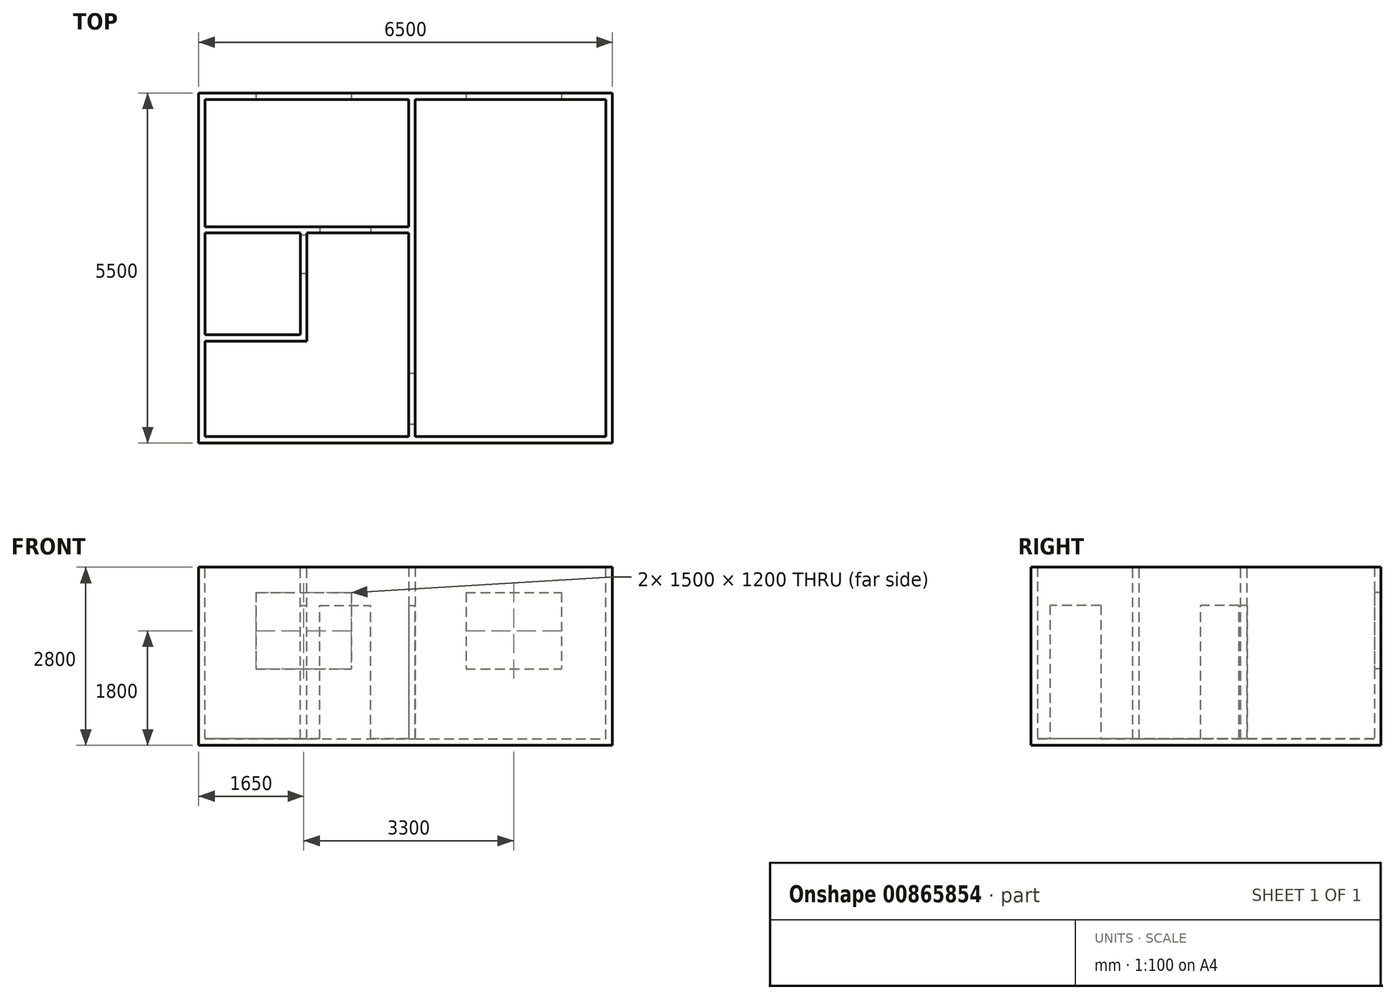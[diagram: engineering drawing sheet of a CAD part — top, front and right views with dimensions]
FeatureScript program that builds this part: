
annotation { "Feature Type Name" : "Feature", "Feature Type Description" : "" }
export const myFeature = defineFeature(function(context is Context, id is Id, definition is map)
    precondition{}
    {
        {
            var Q0;
            Q0=qCreatedBy(makeId("Top.planeOp"),FACE);
            var sketch = newSketch(context, id + "F0", { "sketchPlane" : qUnion([Q0])});
            skLineSegment(sketch, "E0", {"start": v(-6500, 5500) * mm, "end": v(0, 5500) * mm});
            skLineSegment(sketch, "E1", {"start": v(0, 5500) * mm, "end": v(0, 0) * mm});
            skLineSegment(sketch, "E2", {"start": v(0, 0) * mm, "end": v(-6500, 0) * mm});
            skLineSegment(sketch, "E3", {"start": v(-6500, 0) * mm, "end": v(-6500, 5500) * mm});
            skSolve(sketch);
        }
        {
            var Q0;
            Q0=makeQuery(id+"F0.imprint","IMPRINT",FACE,{"disambiguationData":[TD([[makeQuery(id+"F0.imprint","IMPRINT",EDGE,{"derivedFrom":sQuery(id+"F0.wireOp",EDGE,"E0")}),-1.0]])]});
            extrude(context, id + "F1", {"entities" : qUnion([Q0]), "depth" : 2800 * mm, "offsetDistance" : 25 * mm});
        }
        {
            var Q0;
            Q0=makeQuery(id+"F1.opExtrude","CAP_FACE",FACE,{"disambiguationData":[OSD([sQuery(id+"F0.wireOp",EDGE,"E0"),sQuery(id+"F0.wireOp",EDGE,"E1"),sQuery(id+"F0.wireOp",EDGE,"E2"),sQuery(id+"F0.wireOp",EDGE,"E3")])],"isStart":false});
            var sketch = newSketch(context, id + "F2", { "sketchPlane" : qUnion([Q0])});
            skLineSegment(sketch, "E4.bottom", {"start": v(-6400, 5400) * mm, "end": v(-100, 5400) * mm});
            skLineSegment(sketch, "E4.top", {"start": v(-6400, 100) * mm, "end": v(-100, 100) * mm});
            skLineSegment(sketch, "E4.left", {"start": v(-6400, 5400) * mm, "end": v(-6400, 100) * mm});
            skLineSegment(sketch, "E4.right", {"start": v(-100, 5400) * mm, "end": v(-100, 100) * mm});
            skSolve(sketch);
        }
        {
            var Q0;
            Q0=makeQuery(id+"F2.imprint","IMPRINT",FACE,{"disambiguationData":[TD([[makeQuery(id+"F2.imprint","IMPRINT",EDGE,{"derivedFrom":sQuery(id+"F2.wireOp",EDGE,"E4.bottom")}),-1.0]])]});
            extrude(context, id + "F3", {"entities" : qUnion([Q0]), "operationType" : NewBodyOperationType.REMOVE, "oppositeDirection" : true, "depth" : 2700 * mm, "offsetDistance" : 25 * mm});
        }
        {
            var Q0;
            Q0=makeQuery(id+"F3.boolean.opBoolean","COPY",FACE,{"derivedFrom":makeQuery(id+"F3.opExtrude","SWEPT_FACE",FACE,{"disambiguationData":[OSD([sQuery(id+"F2.wireOp",EDGE,"E4.bottom")])]})});
            var sketch = newSketch(context, id + "F4", { "sketchPlane" : qUnion([Q0])});
            skLineSegment(sketch, "E5.bottom", {"start": v(-3200, 2800) * mm, "end": v(-3100, 2800) * mm});
            skLineSegment(sketch, "E5.top", {"start": v(-3200, 100) * mm, "end": v(-3100, 100) * mm});
            skLineSegment(sketch, "E5.left", {"start": v(-3200, 2800) * mm, "end": v(-3200, 100) * mm});
            skLineSegment(sketch, "E5.right", {"start": v(-3100, 2800) * mm, "end": v(-3100, 100) * mm});
            skSolve(sketch);
        }
        {
            var Q0;
            Q0=makeQuery(id+"F4.imprint","IMPRINT",FACE,{"disambiguationData":[TD([[makeQuery(id+"F4.imprint","IMPRINT",EDGE,{"derivedFrom":sQuery(id+"F4.wireOp",EDGE,"E5.bottom")}),-1.0]])]});
            var Q1;
            Q1=makeQuery(id+"F3.boolean.opBoolean","COPY",FACE,{"derivedFrom":makeQuery(id+"F3.opExtrude","SWEPT_FACE",FACE,{"disambiguationData":[OSD([sQuery(id+"F2.wireOp",EDGE,"E4.top")])]})});
            extrude(context, id + "F5", {"entities" : qUnion([Q0]), "operationType" : NewBodyOperationType.ADD, "endBound" : BoundingType.UP_TO_SURFACE, "depth" : 25 * mm, "endBoundEntityFace" : qUnion([Q1]), "offsetDistance" : 25 * mm});
        }
        {
            var Q0;
            Q0=makeQuery(id+"F5.opExtrude","SWEPT_FACE",FACE,{"disambiguationData":[OSD([sQuery(id+"F4.wireOp",EDGE,"E5.right")])]});
            var sketch = newSketch(context, id + "F6", { "sketchPlane" : qUnion([Q0])});
            skLineSegment(sketch, "E6.bottom", {"start": v(300, 100) * mm, "end": v(1100, 100) * mm});
            skLineSegment(sketch, "E6.top", {"start": v(300, 2200) * mm, "end": v(1100, 2200) * mm});
            skLineSegment(sketch, "E6.left", {"start": v(300, 100) * mm, "end": v(300, 2200) * mm});
            skLineSegment(sketch, "E6.right", {"start": v(1100, 100) * mm, "end": v(1100, 2200) * mm});
            skSolve(sketch);
        }
        {
            var Q0;
            Q0=makeQuery(id+"F6.imprint","IMPRINT",FACE,{"disambiguationData":[TD([[makeQuery(id+"F6.imprint","IMPRINT",EDGE,{"derivedFrom":sQuery(id+"F6.wireOp",EDGE,"E6.bottom")}),1.0]])]});
            extrude(context, id + "F7", {"entities" : qUnion([Q0]), "operationType" : NewBodyOperationType.REMOVE, "endBound" : BoundingType.UP_TO_NEXT, "oppositeDirection" : true, "depth" : 25 * mm, "offsetDistance" : 25 * mm});
        }
        {
            var Q0;
            Q0=makeQuery(id+"F3.boolean.opBoolean","COPY",FACE,{"derivedFrom":makeQuery(id+"F3.opExtrude","SWEPT_FACE",FACE,{"disambiguationData":[OSD([sQuery(id+"F2.wireOp",EDGE,"E4.left")])]})});
            var sketch = newSketch(context, id + "F8", { "sketchPlane" : qUnion([Q0])});
            skLineSegment(sketch, "E7.bottom", {"start": v(3300, 100) * mm, "end": v(3400, 100) * mm});
            skLineSegment(sketch, "E7.top", {"start": v(3300, 2800) * mm, "end": v(3400, 2800) * mm});
            skLineSegment(sketch, "E7.left", {"start": v(3300, 100) * mm, "end": v(3300, 2800) * mm});
            skLineSegment(sketch, "E7.right", {"start": v(3400, 100) * mm, "end": v(3400, 2800) * mm});
            skSolve(sketch);
        }
        {
            var Q0;
            Q0=makeQuery(id+"F8.imprint","IMPRINT",FACE,{"disambiguationData":[TD([[makeQuery(id+"F8.imprint","IMPRINT",EDGE,{"derivedFrom":sQuery(id+"F8.wireOp",EDGE,"E7.bottom")}),-1.0]])]});
            extrude(context, id + "F9", {"entities" : qUnion([Q0]), "operationType" : NewBodyOperationType.ADD, "endBound" : BoundingType.UP_TO_NEXT, "depth" : 25 * mm, "offsetDistance" : 25 * mm});
        }
        {
            var Q0;
            Q0=makeQuery(id+"F9.opExtrude","SWEPT_FACE",FACE,{"disambiguationData":[OSD([sQuery(id+"F8.wireOp",EDGE,"E7.left")])]});
            var sketch = newSketch(context, id + "F10", { "sketchPlane" : qUnion([Q0])});
            skLineSegment(sketch, "E8.bottom", {"start": v(-4600, 100) * mm, "end": v(-3800, 100) * mm});
            skLineSegment(sketch, "E8.top", {"start": v(-4600, 2200) * mm, "end": v(-3800, 2200) * mm});
            skLineSegment(sketch, "E8.left", {"start": v(-4600, 100) * mm, "end": v(-4600, 2200) * mm});
            skLineSegment(sketch, "E8.right", {"start": v(-3800, 100) * mm, "end": v(-3800, 2200) * mm});
            skSolve(sketch);
        }
        {
            var Q0;
            Q0=makeQuery(id+"F10.imprint","IMPRINT",FACE,{"disambiguationData":[TD([[makeQuery(id+"F10.imprint","IMPRINT",EDGE,{"derivedFrom":sQuery(id+"F10.wireOp",EDGE,"E8.bottom")}),-1.0]])]});
            extrude(context, id + "F11", {"entities" : qUnion([Q0]), "operationType" : NewBodyOperationType.REMOVE, "endBound" : BoundingType.UP_TO_NEXT, "oppositeDirection" : true, "depth" : 25 * mm, "offsetDistance" : 25 * mm});
        }
        {
            var Q0;
            Q0=makeQuery(id+"F9.opExtrude","SWEPT_FACE",FACE,{"disambiguationData":[OSD([sQuery(id+"F8.wireOp",EDGE,"E7.left")])]});
            var sketch = newSketch(context, id + "F12", { "sketchPlane" : qUnion([Q0])});
            skLineSegment(sketch, "E9.bottom", {"start": v(-4800, 100) * mm, "end": v(-4900, 100) * mm});
            skLineSegment(sketch, "E9.top", {"start": v(-4800, 2800) * mm, "end": v(-4900, 2800) * mm});
            skLineSegment(sketch, "E9.left", {"start": v(-4800, 100) * mm, "end": v(-4800, 2800) * mm});
            skLineSegment(sketch, "E9.right", {"start": v(-4900, 100) * mm, "end": v(-4900, 2800) * mm});
            skSolve(sketch);
        }
        {
            var Q0;
            Q0=makeQuery(id+"F12.imprint","IMPRINT",FACE,{"disambiguationData":[TD([[makeQuery(id+"F12.imprint","IMPRINT",EDGE,{"derivedFrom":sQuery(id+"F12.wireOp",EDGE,"E9.bottom")}),-1.0]])]});
            extrude(context, id + "F13", {"entities" : qUnion([Q0]), "operationType" : NewBodyOperationType.ADD, "depth" : 1700 * mm, "offsetDistance" : 25 * mm});
        }
        {
            var Q0;
            Q0=makeQuery(id+"F13.opExtrude","SWEPT_FACE",FACE,{"disambiguationData":[OSD([sQuery(id+"F12.wireOp",EDGE,"E9.right")])]});
            var sketch = newSketch(context, id + "F14", { "sketchPlane" : qUnion([Q0])});
            skLineSegment(sketch, "E10", {"start": v(-1700, 100) * mm, "end": v(-1700, 2800) * mm});
            skSolve(sketch);
        }
        {
            var Q0;
            {var subQ0=sQuery(id+"F14.wireOp",EDGE,"E10");Q0=makeQuery(id+"F14.imprint","IMPRINT",FACE,{"disambiguationData":[TD([[makeQuery(id+"F14.imprint","IMPRINT",EDGE,{"derivedFrom":subQ0}),-1.0]])]});}
            extrude(context, id + "F15", {"entities" : qUnion([Q0]), "operationType" : NewBodyOperationType.ADD, "endBound" : BoundingType.UP_TO_NEXT, "depth" : 25 * mm, "offsetDistance" : 25 * mm});
        }
        {
            var Q0;
            {var subQ0=sQuery(id+"F2.wireOp",EDGE,"E4.right");var subQ1=sQuery(id+"F2.wireOp",EDGE,"E4.bottom");Q0=makeQuery(id+"F5.boolean.opBoolean","SPLIT",FACE,{"disambiguationData":[TD([makeQuery(id+"F3.boolean.opBoolean","COPY",FACE,{"derivedFrom":makeQuery(id+"F3.opExtrude","SWEPT_FACE",FACE,{"disambiguationData":[OSD([subQ0])]})})])],"derivedFrom":makeQuery(id+"F3.boolean.opBoolean","COPY",FACE,{"derivedFrom":makeQuery(id+"F3.opExtrude","SWEPT_FACE",FACE,{"disambiguationData":[OSD([subQ1])]})})});}
            var sketch = newSketch(context, id + "F16", { "sketchPlane" : qUnion([Q0])});
            skLineSegment(sketch, "E11.bottom", {"start": v(-2300, 2400) * mm, "end": v(-800, 2400) * mm});
            skLineSegment(sketch, "E11.top", {"start": v(-2300, 1200) * mm, "end": v(-800, 1200) * mm});
            skLineSegment(sketch, "E11.left", {"start": v(-2300, 2400) * mm, "end": v(-2300, 1200) * mm});
            skLineSegment(sketch, "E11.right", {"start": v(-800, 2400) * mm, "end": v(-800, 1200) * mm});
            skSolve(sketch);
        }
        {
            var Q0;
            Q0=makeQuery(id+"F16.imprint","IMPRINT",FACE,{"disambiguationData":[TD([[makeQuery(id+"F16.imprint","IMPRINT",EDGE,{"derivedFrom":sQuery(id+"F16.wireOp",EDGE,"E11.bottom")}),-1.0]])]});
            extrude(context, id + "F17", {"entities" : qUnion([Q0]), "operationType" : NewBodyOperationType.REMOVE, "endBound" : BoundingType.UP_TO_NEXT, "oppositeDirection" : true, "depth" : 25 * mm, "offsetDistance" : 25 * mm});
        }
        {
            var Q0;
            {var subQ0=sQuery(id+"F2.wireOp",EDGE,"E4.left");var subQ1=sQuery(id+"F2.wireOp",EDGE,"E4.bottom");Q0=makeQuery(id+"F5.boolean.opBoolean","SPLIT",FACE,{"disambiguationData":[TD([makeQuery(id+"F3.boolean.opBoolean","COPY",FACE,{"derivedFrom":makeQuery(id+"F3.opExtrude","SWEPT_FACE",FACE,{"disambiguationData":[OSD([subQ0])]})})])],"derivedFrom":makeQuery(id+"F3.boolean.opBoolean","COPY",FACE,{"derivedFrom":makeQuery(id+"F3.opExtrude","SWEPT_FACE",FACE,{"disambiguationData":[OSD([subQ1])]})})});}
            var sketch = newSketch(context, id + "F18", { "sketchPlane" : qUnion([Q0])});
            skLineSegment(sketch, "E12.bottom", {"start": v(-5600, 2400) * mm, "end": v(-4100, 2400) * mm});
            skLineSegment(sketch, "E12.top", {"start": v(-5600, 1200) * mm, "end": v(-4100, 1200) * mm});
            skLineSegment(sketch, "E12.left", {"start": v(-5600, 2400) * mm, "end": v(-5600, 1200) * mm});
            skLineSegment(sketch, "E12.right", {"start": v(-4100, 2400) * mm, "end": v(-4100, 1200) * mm});
            skSolve(sketch);
        }
        {
            var Q0;
            Q0=makeQuery(id+"F18.imprint","IMPRINT",FACE,{"disambiguationData":[TD([[makeQuery(id+"F18.imprint","IMPRINT",EDGE,{"derivedFrom":sQuery(id+"F18.wireOp",EDGE,"E12.bottom")}),-1.0]])]});
            extrude(context, id + "F19", {"entities" : qUnion([Q0]), "operationType" : NewBodyOperationType.REMOVE, "endBound" : BoundingType.UP_TO_NEXT, "oppositeDirection" : true, "depth" : 25 * mm, "offsetDistance" : 25 * mm});
        }
        {
            var Q0;
            Q0=makeQuery(id+"F13.opExtrude","SWEPT_FACE",FACE,{"disambiguationData":[OSD([sQuery(id+"F12.wireOp",EDGE,"E9.left")])]});
            var sketch = newSketch(context, id + "F20", { "sketchPlane" : qUnion([Q0])});
            skLineSegment(sketch, "E13.bottom", {"start": v(3270, 100) * mm, "end": v(2670, 100) * mm});
            skLineSegment(sketch, "E13.top", {"start": v(3270, 2200) * mm, "end": v(2670, 2200) * mm});
            skLineSegment(sketch, "E13.left", {"start": v(3270, 100) * mm, "end": v(3270, 2200) * mm});
            skLineSegment(sketch, "E13.right", {"start": v(2670, 100) * mm, "end": v(2670, 2200) * mm});
            skSolve(sketch);
        }
        {
            var Q0;
            Q0=makeQuery(id+"F20.imprint","IMPRINT",FACE,{"disambiguationData":[TD([[makeQuery(id+"F20.imprint","IMPRINT",EDGE,{"derivedFrom":sQuery(id+"F20.wireOp",EDGE,"E13.bottom")}),1.0]])]});
            extrude(context, id + "F21", {"entities" : qUnion([Q0]), "operationType" : NewBodyOperationType.REMOVE, "endBound" : BoundingType.UP_TO_NEXT, "oppositeDirection" : true, "depth" : 25 * mm, "offsetDistance" : 25 * mm});
        }
    });
